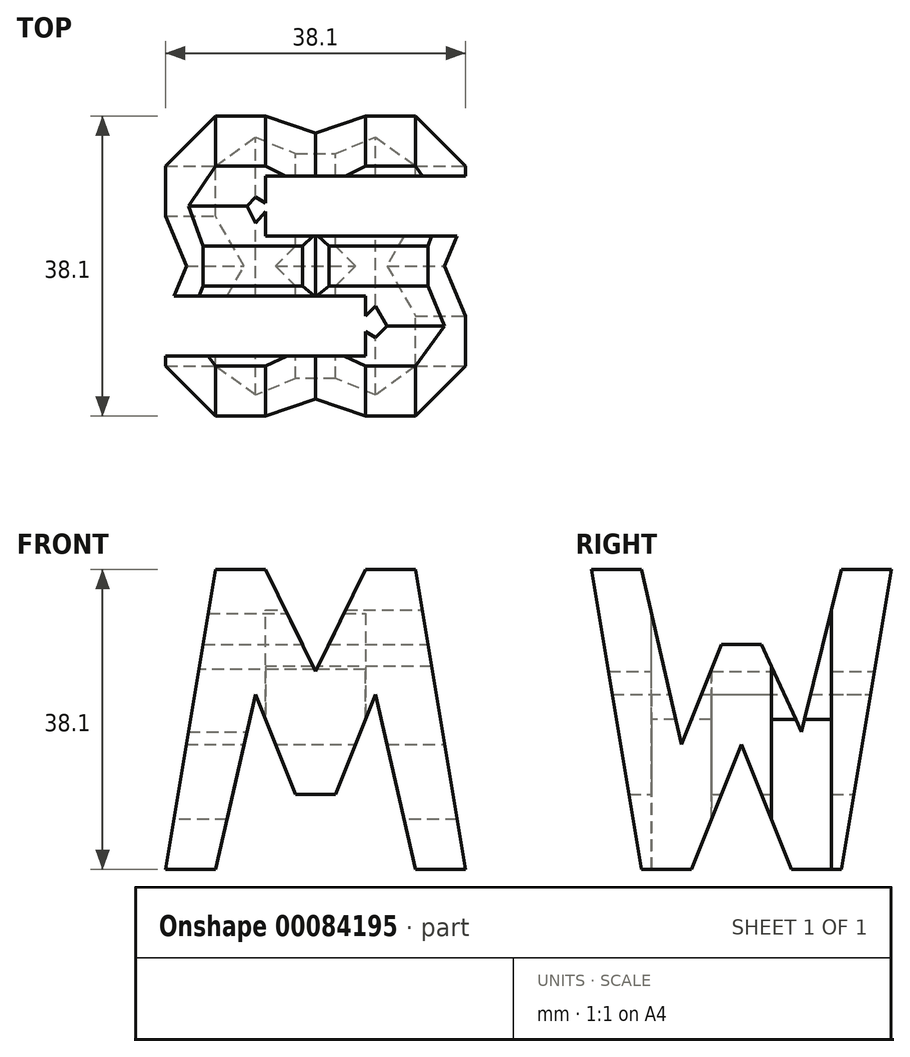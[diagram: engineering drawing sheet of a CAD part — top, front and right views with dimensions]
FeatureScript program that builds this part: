
annotation { "Feature Type Name" : "Feature", "Feature Type Description" : "" }
export const myFeature = defineFeature(function(context is Context, id is Id, definition is map)
    precondition{}
    {
        {
            var Q0;
            Q0=qCreatedBy(makeId("Front.planeOp"),FACE);
            var sketch = newSketch(context, id + "F0", { "sketchPlane" : qUnion([Q0])});
            skLineSegment(sketch, "E0", {"start": v(0, 0) * mm, "end": v(0, 38.1) * mm});
            skLineSegment(sketch, "E1", {"start": v(0, 38.1) * mm, "end": v(38.1, 38.1) * mm});
            skLineSegment(sketch, "E2", {"start": v(38.1, 38.1) * mm, "end": v(38.1, 0) * mm});
            skLineSegment(sketch, "E3", {"start": v(38.1, 0) * mm, "end": v(0, 0) * mm});
            skSolve(sketch);
        }
        {
            var Q0;
            Q0=makeQuery(id+"F0.imprint","IMPRINT",FACE,{"disambiguationData":[TD([[makeQuery(id+"F0.imprint","IMPRINT",EDGE,{"derivedFrom":sQuery(id+"F0.wireOp",EDGE,"E0")}),-1.0]])]});
            extrude(context, id + "F1", {"entities" : qUnion([Q0]), "depth" : 38.1 * mm});
        }
        {
            var Q0;
            Q0=qCreatedBy(makeId("Right.planeOp"),FACE);
            cPlane(context, id + "F2", {"entities" : qUnion([Q0]), "cplaneType" : CPlaneType.OFFSET, "offset" : 38.1 * mm, "width" : 152.4 * mm, "height" : 152.4 * mm});
        }
        {
            var Q0;
            Q0=qCreatedBy(makeId("Top.planeOp"),FACE);
            cPlane(context, id + "F3", {"entities" : qUnion([Q0]), "cplaneType" : CPlaneType.OFFSET, "offset" : 38.1 * mm, "width" : 152.4 * mm, "height" : 152.4 * mm});
        }
        {
            var Q0;
            Q0=qCreatedBy(id+"F2.planeOp",FACE);
            var sketch = newSketch(context, id + "F4", { "sketchPlane" : qUnion([Q0])});
            skLineSegment(sketch, "E4", {"start": v(0, 0) * mm, "end": v(0, 38.1) * mm});
            skLineSegment(sketch, "E5", {"start": v(0, 38.1) * mm, "end": v(-38.1, 38.1) * mm});
            skLineSegment(sketch, "E6", {"start": v(-38.1, 38.1) * mm, "end": v(-38.1, 0) * mm});
            skLineSegment(sketch, "E7", {"start": v(-38.1, 0) * mm, "end": v(0, 0) * mm});
            skLineSegment(sketch, "E8", {"start": v(-38.1, 38.1) * mm, "end": v(-31.75, 0) * mm});
            skLineSegment(sketch, "E9", {"start": v(-25.4, 0) * mm, "end": v(-19.05, 15.88) * mm});
            skLineSegment(sketch, "E10", {"start": v(-19.05, 15.88) * mm, "end": v(-12.7, 0) * mm});
            skLineSegment(sketch, "E11", {"start": v(-6.35, 0) * mm, "end": v(0, 38.1) * mm});
            skLineSegment(sketch, "E12", {"start": v(-31.75, 38.1) * mm, "end": v(-26.67, 15.88) * mm});
            skLineSegment(sketch, "E13", {"start": v(-26.67, 15.88) * mm, "end": v(-21.59, 28.58) * mm});
            skLineSegment(sketch, "E14", {"start": v(-21.59, 28.58) * mm, "end": v(-16.5, 28.58) * mm});
            skLineSegment(sketch, "E15", {"start": v(-16.51, 28.58) * mm, "end": v(-11.43, 17.48) * mm});
            skLineSegment(sketch, "E16", {"start": v(-11.43, 17.48) * mm, "end": v(-6.35, 38.1) * mm});
            skSolve(sketch);
        }
        {
            var Q0;
            {var subQ0=sQuery(id+"F4.wireOp",EDGE,"E4");Q0=makeQuery(id+"F4.imprint","IMPRINT",FACE,{"disambiguationData":[TD([[makeQuery(id+"F4.imprint","IMPRINT",EDGE,{"derivedFrom":subQ0}),1.0]])]});}
            var Q1;
            {var subQ0=sQuery(id+"F4.wireOp",EDGE,"E12");Q1=makeQuery(id+"F4.imprint","IMPRINT",FACE,{"disambiguationData":[TD([[makeQuery(id+"F4.imprint","IMPRINT",EDGE,{"derivedFrom":subQ0}),1.0]])]});}
            var Q2;
            {var subQ0=sQuery(id+"F4.wireOp",EDGE,"E6");Q2=makeQuery(id+"F4.imprint","IMPRINT",FACE,{"disambiguationData":[TD([[makeQuery(id+"F4.imprint","IMPRINT",EDGE,{"derivedFrom":subQ0}),1.0]])]});}
            var Q3;
            {var subQ0=sQuery(id+"F4.wireOp",EDGE,"E9");Q3=makeQuery(id+"F4.imprint","IMPRINT",FACE,{"disambiguationData":[TD([[makeQuery(id+"F4.imprint","IMPRINT",EDGE,{"derivedFrom":subQ0}),-1.0]])]});}
            extrude(context, id + "F5", {"entities" : qUnion([Q0, Q1, Q2, Q3]), "operationType" : NewBodyOperationType.REMOVE, "oppositeDirection" : true, "depth" : 38.1 * mm});
        }
        {
            var Q0;
            Q0=qCreatedBy(makeId("Front.planeOp"),FACE);
            var sketch = newSketch(context, id + "F6", { "sketchPlane" : qUnion([Q0])});
            skLineSegment(sketch, "E17", {"start": v(0, 38.1) * mm, "end": v(0, 0) * mm});
            skLineSegment(sketch, "E18", {"start": v(0, 0) * mm, "end": v(38.1, 0) * mm});
            skLineSegment(sketch, "E19", {"start": v(38.1, 0) * mm, "end": v(38.1, 38.1) * mm});
            skLineSegment(sketch, "E20", {"start": v(38.1, 38.1) * mm, "end": v(0, 38.1) * mm});
            skLineSegment(sketch, "E21", {"start": v(6.35, 38.1) * mm, "end": v(0, 0) * mm});
            skLineSegment(sketch, "E22", {"start": v(6.35, 0) * mm, "end": v(11.43, 22.23) * mm});
            skLineSegment(sketch, "E23", {"start": v(11.43, 22.23) * mm, "end": v(16.51, 9.53) * mm});
            skLineSegment(sketch, "E24", {"start": v(16.51, 9.53) * mm, "end": v(21.59, 9.53) * mm});
            skLineSegment(sketch, "E25", {"start": v(21.59, 9.52) * mm, "end": v(26.67, 22.22) * mm});
            skLineSegment(sketch, "E26", {"start": v(26.67, 22.22) * mm, "end": v(31.75, 0) * mm});
            skLineSegment(sketch, "E27", {"start": v(12.7, 38.1) * mm, "end": v(19.05, 25.14) * mm});
            skLineSegment(sketch, "E28", {"start": v(19.05, 25.14) * mm, "end": v(25.4, 38.1) * mm});
            skLineSegment(sketch, "E29", {"start": v(31.75, 38.1) * mm, "end": v(38.1, 0) * mm});
            skSolve(sketch);
        }
        {
            var Q0;
            {var subQ0=sQuery(id+"F6.wireOp",EDGE,"E22");Q0=makeQuery(id+"F6.imprint","IMPRINT",FACE,{"disambiguationData":[TD([[makeQuery(id+"F6.imprint","IMPRINT",EDGE,{"derivedFrom":subQ0}),-1.0]])]});}
            var Q1;
            {var subQ0=sQuery(id+"F6.wireOp",EDGE,"E19");Q1=makeQuery(id+"F6.imprint","IMPRINT",FACE,{"disambiguationData":[TD([[makeQuery(id+"F6.imprint","IMPRINT",EDGE,{"derivedFrom":subQ0}),1.0]])]});}
            var Q2;
            {var subQ0=sQuery(id+"F6.wireOp",EDGE,"E27");Q2=makeQuery(id+"F6.imprint","IMPRINT",FACE,{"disambiguationData":[TD([[makeQuery(id+"F6.imprint","IMPRINT",EDGE,{"derivedFrom":subQ0}),1.0]])]});}
            var Q3;
            {var subQ0=sQuery(id+"F6.wireOp",EDGE,"E17");Q3=makeQuery(id+"F6.imprint","IMPRINT",FACE,{"disambiguationData":[TD([[makeQuery(id+"F6.imprint","IMPRINT",EDGE,{"derivedFrom":subQ0}),1.0]])]});}
            extrude(context, id + "F7", {"entities" : qUnion([Q0, Q1, Q2, Q3]), "operationType" : NewBodyOperationType.REMOVE, "depth" : 38.1 * mm});
        }
        {
            var Q0;
            Q0=qCreatedBy(id+"F3.planeOp",FACE);
            var sketch = newSketch(context, id + "F8", { "sketchPlane" : qUnion([Q0])});
            skLineSegment(sketch, "E30", {"start": v(0, 0) * mm, "end": v(0, -38.1) * mm});
            skLineSegment(sketch, "E31", {"start": v(0, -38.1) * mm, "end": v(38.1, -38.1) * mm});
            skLineSegment(sketch, "E32", {"start": v(38.1, -38.1) * mm, "end": v(38.1, 0) * mm});
            skLineSegment(sketch, "E33", {"start": v(38.1, 0) * mm, "end": v(0, 0) * mm});
            skLineSegment(sketch, "E34", {"start": v(38.1, -7.62) * mm, "end": v(12.7, -7.62) * mm});
            skLineSegment(sketch, "E35", {"start": v(12.7, -7.62) * mm, "end": v(12.7, -15.24) * mm});
            skLineSegment(sketch, "E36", {"start": v(12.7, -15.24) * mm, "end": v(38.1, -15.24) * mm});
            skLineSegment(sketch, "E37", {"start": v(0, -22.86) * mm, "end": v(25.4, -22.86) * mm});
            skLineSegment(sketch, "E38", {"start": v(25.4, -22.86) * mm, "end": v(25.4, -30.48) * mm});
            skLineSegment(sketch, "E39", {"start": v(25.4, -30.48) * mm, "end": v(0, -30.48) * mm});
            skSolve(sketch);
        }
        {
            var Q0;
            {var subQ0=sQuery(id+"F8.wireOp",EDGE,"E34");Q0=makeQuery(id+"F8.imprint","IMPRINT",FACE,{"disambiguationData":[TD([[makeQuery(id+"F8.imprint","IMPRINT",EDGE,{"derivedFrom":subQ0}),1.0]])]});}
            var Q1;
            {var subQ0=sQuery(id+"F8.wireOp",EDGE,"E37");Q1=makeQuery(id+"F8.imprint","IMPRINT",FACE,{"disambiguationData":[TD([[makeQuery(id+"F8.imprint","IMPRINT",EDGE,{"derivedFrom":subQ0}),-1.0]])]});}
            extrude(context, id + "F9", {"entities" : qUnion([Q0, Q1]), "operationType" : NewBodyOperationType.REMOVE, "oppositeDirection" : true, "depth" : 38.1 * mm});
        }
    });
